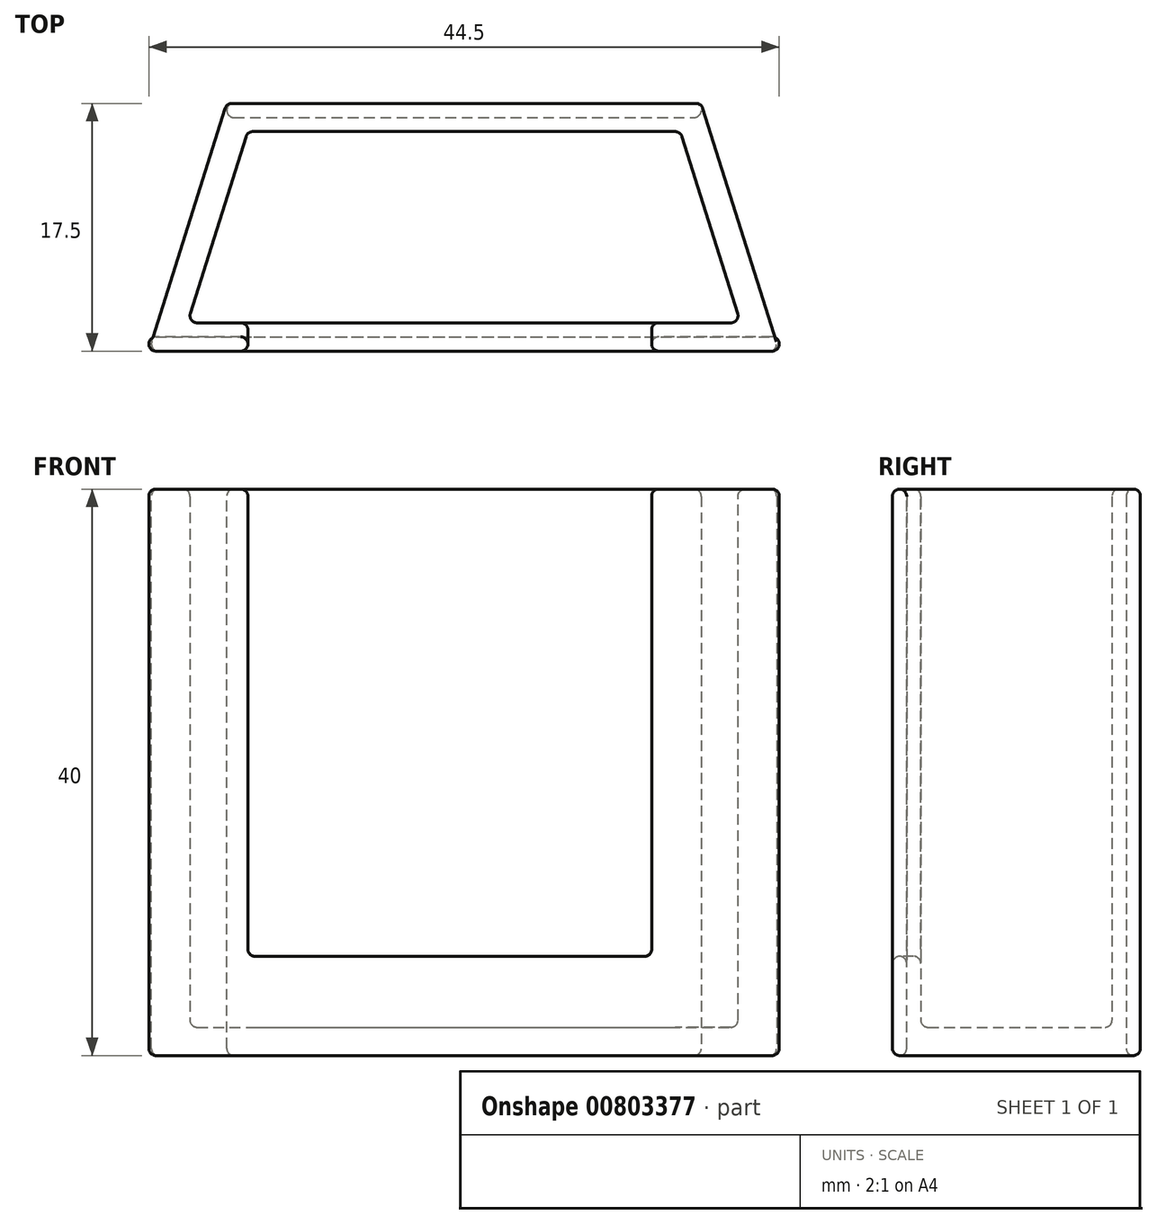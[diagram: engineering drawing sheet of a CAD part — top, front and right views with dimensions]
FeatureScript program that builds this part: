
annotation { "Feature Type Name" : "Feature", "Feature Type Description" : "" }
export const myFeature = defineFeature(function(context is Context, id is Id, definition is map)
    precondition{}
    {
        {
            var Q0;
            Q0=qCreatedBy(makeId("Front.planeOp"),FACE);
            var sketch = newSketch(context, id + "F0", { "sketchPlane" : qUnion([Q0])});
            skLineSegment(sketch, "E0", {"start": v(0, 0) * mm, "end": v(0, 40) * mm});
            skLineSegment(sketch, "E1", {"start": v(0, 0) * mm, "end": v(44.5, 0) * mm});
            skLineSegment(sketch, "E2", {"start": v(44.5, 0) * mm, "end": v(44.5, 40) * mm});
            skLineSegment(sketch, "E3", {"start": v(0, 40) * mm, "end": v(1, 40) * mm});
            skLineSegment(sketch, "E4", {"start": v(44.5, 40) * mm, "end": v(43.5, 40) * mm});
            skLineSegment(sketch, "E5", {"start": v(1, 40) * mm, "end": v(1, 1) * mm});
            skLineSegment(sketch, "E6", {"start": v(1, 1) * mm, "end": v(43.5, 1) * mm});
            skLineSegment(sketch, "E7", {"start": v(43.5, 1) * mm, "end": v(43.5, 40) * mm});
            skPoint(sketch, "E8.end.orphan", {"position": v(32.5, 40) * mm});
            skPoint(sketch, "E9.end.orphan", {"position": v(32.5, 10) * mm});
            skLineSegment(sketch, "E10", {"start": v(44.5, 40) * mm, "end": v(0, 40) * mm});
            skSolve(sketch);
        }
        {
            var Q0;
            Q0 = qSketchRegion(id + "F0", true);
            extrude(context, id + "F1", {"entities" : qUnion([Q0]), "depth" : 1 * mm, "offsetDistance" : 25 * mm});
        }
        {
            var Q0;
            Q0=qCreatedBy(makeId("Front.planeOp"),FACE);
            cPlane(context, id + "F2", {"entities" : qUnion([Q0]), "cplaneType" : CPlaneType.OFFSET, "offset" : 16.5 * mm, "oppositeDirection" : true, "width" : 150 * mm, "height" : 150 * mm});
        }
        {
            var Q0;
            Q0=qCreatedBy(id+"F2.planeOp",FACE);
            var sketch = newSketch(context, id + "F3", { "sketchPlane" : qUnion([Q0])});
            skLineSegment(sketch, "E11", {"start": v(22.25, 0) * mm, "end": v(22.25, 43.45) * mm, "construction": true});
            skLineSegment(sketch, "E12", {"start": v(5.5, 0) * mm, "end": v(39, 0) * mm});
            skPoint(sketch, "E13.orphan", {"position": v(0, 0) * mm});
            skPoint(sketch, "E14.orphan", {"position": v(44.5, 0) * mm});
            skLineSegment(sketch, "E15", {"start": v(5.5, 0) * mm, "end": v(5.5, 40) * mm});
            skLineSegment(sketch, "E16", {"start": v(5.5, 40) * mm, "end": v(39, 40) * mm});
            skLineSegment(sketch, "E17", {"start": v(39, 40) * mm, "end": v(39, 0) * mm});
            skSolve(sketch);
        }
        {
            var Q0;
            Q0 = qSketchRegion(id + "F3", true);
            extrude(context, id + "F4", {"entities" : qUnion([Q0]), "depth" : 1 * mm, "offsetDistance" : 25 * mm});
        }
        {
            var Q0;
            Q0=makeQuery(id+"F4.opExtrude","CAP_FACE",FACE,{"disambiguationData":[OSD([sQuery(id+"F3.wireOp",EDGE,"E12"),sQuery(id+"F3.wireOp",EDGE,"E15"),sQuery(id+"F3.wireOp",EDGE,"E16"),sQuery(id+"F3.wireOp",EDGE,"E17")])],"isStart":true});
            var Q1;
            Q1=makeQuery(id+"F1.opExtrude","CAP_FACE",FACE,{"disambiguationData":[OSD([sQuery(id+"F0.wireOp",EDGE,"E0"),sQuery(id+"F0.wireOp",EDGE,"E1"),sQuery(id+"F0.wireOp",EDGE,"E2"),sQuery(id+"F0.wireOp",EDGE,"E10")])],"isStart":false});
            loft(context, id + "F5", {"sheetProfilesArray" : [{ "sheetProfileEntities" : qUnion([Q0]) }, { "sheetProfileEntities" : qUnion([Q1]) }]});
        }
        {
            var Q0;
            Q0=makeQuery(id+"F5.opLoft","SWEPT_FACE",FACE,{"disambiguationData":[OSD([sQuery(id+"F0.wireOp",EDGE,"E0"),sQuery(id+"F0.wireOp",EDGE,"E2"),sQuery(id+"F0.wireOp",EDGE,"E10"),sQuery(id+"F3.wireOp",EDGE,"E15"),sQuery(id+"F3.wireOp",EDGE,"E16"),sQuery(id+"F3.wireOp",EDGE,"E17")])]});
            shell(context, id + "F6", {"entities" : qUnion([Q0]), "thickness" : 2 * mm});
        }
        {
            var Q0;
            Q0=makeQuery(id+"F1.opExtrude","CAP_FACE",FACE,{"disambiguationData":[OSD([sQuery(id+"F0.wireOp",EDGE,"E0"),sQuery(id+"F0.wireOp",EDGE,"E1"),sQuery(id+"F0.wireOp",EDGE,"E2"),sQuery(id+"F0.wireOp",EDGE,"E10")])],"isStart":false});
            var sketch = newSketch(context, id + "F7", { "sketchPlane" : qUnion([Q0])});
            skLineSegment(sketch, "E18", {"start": v(7, 40) * mm, "end": v(7, 7) * mm});
            skLineSegment(sketch, "E19", {"start": v(7, 7) * mm, "end": v(35.5, 7) * mm});
            skLineSegment(sketch, "E20", {"start": v(35.5, 7) * mm, "end": v(35.5, 40) * mm});
            skLineSegment(sketch, "E21", {"start": v(7, 40) * mm, "end": v(35.5, 40) * mm});
            skPoint(sketch, "E22.0.end.orphan", {"position": v(0, 40) * mm});
            skPoint(sketch, "E22.0.start.orphan", {"position": v(0, 0) * mm});
            skPoint(sketch, "E23.0.end.orphan", {"position": v(44.5, 40) * mm});
            skPoint(sketch, "E23.0.start.orphan", {"position": v(44.5, 0) * mm});
            skSolve(sketch);
        }
        {
            var Q0;
            Q0=makeQuery(id+"F7.imprint","IMPRINT",FACE,{"disambiguationData":[TD([[makeQuery(id+"F7.imprint","IMPRINT",EDGE,{"derivedFrom":sQuery(id+"F7.wireOp",EDGE,"E18")}),1.0]])]});
            var sketch = newSketch(context, id + "F8", { "sketchPlane" : qUnion([Q0])});
            skLineSegment(sketch, "E24.0", {"start": v(35.5, 7) * mm, "end": v(35.5, 40) * mm});
            skLineSegment(sketch, "E24.1", {"start": v(7, 7) * mm, "end": v(35.5, 7) * mm});
            skLineSegment(sketch, "E24.2", {"start": v(7, 40) * mm, "end": v(7, 7) * mm});
            skLineSegment(sketch, "E24.3", {"start": v(7, 40) * mm, "end": v(35.5, 40) * mm});
            skSolve(sketch);
        }
        {
            var Q0;
            Q0 = qSketchRegion(id + "F8", true);
            extrude(context, id + "F9", {"entities" : qUnion([Q0]), "operationType" : NewBodyOperationType.REMOVE, "depth" : -5 * mm, "offsetDistance" : 25 * mm});
        }
        {
            var Q0;
            Q0=makeQuery(id+"F1.opExtrude","CAP_EDGE",EDGE,{"disambiguationData":[OSD([sQuery(id+"F0.wireOp",EDGE,"E1")])],"isStart":false});
            var Q1;
            Q1=makeQuery(id+"F1.opExtrude","SWEPT_FACE",FACE,{"disambiguationData":[OSD([sQuery(id+"F0.wireOp",EDGE,"E1")])]});
            var Q2;
            Q2=makeQuery(id+"F5.opLoft","SWEPT_EDGE",EDGE,{"disambiguationData":[OSD([sQuery(id+"F0.wireOp",EDGE,"E1"),sQuery(id+"F0.wireOp",EDGE,"E2"),sQuery(id+"F3.wireOp",EDGE,"E12"),sQuery(id+"F3.wireOp",EDGE,"E17")])]});
            var Q3;
            Q3=makeQuery(id+"F5.opLoft","SWEPT_FACE",FACE,{"disambiguationData":[OSD([sQuery(id+"F0.wireOp",EDGE,"E0"),sQuery(id+"F0.wireOp",EDGE,"E2"),sQuery(id+"F0.wireOp",EDGE,"E10"),sQuery(id+"F3.wireOp",EDGE,"E15"),sQuery(id+"F3.wireOp",EDGE,"E16"),sQuery(id+"F3.wireOp",EDGE,"E17")])]});
            var Q4;
            Q4=makeQuery(id+"F5.opLoft","SWEPT_FACE",FACE,{"disambiguationData":[OSD([sQuery(id+"F0.wireOp",EDGE,"E0"),sQuery(id+"F0.wireOp",EDGE,"E1"),sQuery(id+"F0.wireOp",EDGE,"E10"),sQuery(id+"F3.wireOp",EDGE,"E12"),sQuery(id+"F3.wireOp",EDGE,"E15"),sQuery(id+"F3.wireOp",EDGE,"E16")])]});
            var Q5;
            Q5=makeQuery(id+"F5.opLoft","SWEPT_EDGE",EDGE,{"disambiguationData":[OSD([sQuery(id+"F0.wireOp",EDGE,"E0"),sQuery(id+"F0.wireOp",EDGE,"E10"),sQuery(id+"F3.wireOp",EDGE,"E15"),sQuery(id+"F3.wireOp",EDGE,"E16")])]});
            var Q6;
            Q6=makeQuery(id+"F5.opLoft","MID_CAP_EDGE",EDGE,{"disambiguationData":[OSD([sQuery(id+"F0.wireOp",EDGE,"E0"),sQuery(id+"F0.wireOp",EDGE,"E1"),sQuery(id+"F0.wireOp",EDGE,"E2")])],"capPos":1.0});
            var Q7;
            Q7=makeQuery(id+"F5.opLoft","SWEPT_FACE",FACE,{"disambiguationData":[OSD([sQuery(id+"F0.wireOp",EDGE,"E0"),sQuery(id+"F0.wireOp",EDGE,"E1"),sQuery(id+"F0.wireOp",EDGE,"E2"),sQuery(id+"F3.wireOp",EDGE,"E12"),sQuery(id+"F3.wireOp",EDGE,"E15"),sQuery(id+"F3.wireOp",EDGE,"E17")])]});
            var Q8;
            Q8=makeQuery(id+"F1.opExtrude","CAP_EDGE",EDGE,{"disambiguationData":[OSD([sQuery(id+"F0.wireOp",EDGE,"E1")])],"isStart":true});
            var Q9;
            Q9=makeQuery(id+"F1.opExtrude","SWEPT_FACE",FACE,{"disambiguationData":[OSD([sQuery(id+"F0.wireOp",EDGE,"E0")])]});
            var Q10;
            Q10=makeQuery(id+"F1.opExtrude","SWEPT_FACE",FACE,{"disambiguationData":[OSD([sQuery(id+"F0.wireOp",EDGE,"E2")])]});
            var Q11;
            Q11=makeQuery(id+"F1.opExtrude","CAP_FACE",FACE,{"disambiguationData":[OSD([sQuery(id+"F0.wireOp",EDGE,"E0"),sQuery(id+"F0.wireOp",EDGE,"E1"),sQuery(id+"F0.wireOp",EDGE,"E2"),sQuery(id+"F0.wireOp",EDGE,"E10")])],"isStart":false});
            var Q12;
            {var subQ0=sQuery(id+"F0.wireOp",EDGE,"E10");Q12=makeQuery(id+"F9.boolean.opBoolean","COPY",FACE,{"disambiguationData":[TD([makeQuery(id+"F1.opExtrude","SWEPT_FACE",FACE,{"disambiguationData":[OSD([subQ0])]})])],"derivedFrom":makeQuery(id+"F9.opExtrude","SWEPT_FACE",FACE,{"disambiguationData":[OSD([sQuery(id+"F8.wireOp",EDGE,"E24.0")])]})});}
            var Q13;
            {var subQ0=sQuery(id+"F0.wireOp",EDGE,"E10");var subQ1=sQuery(id+"F0.wireOp",EDGE,"E2");var subQ2=sQuery(id+"F0.wireOp",EDGE,"E1");var subQ3=sQuery(id+"F0.wireOp",EDGE,"E0");Q13=makeQuery(id+"F9.boolean.opBoolean","COPY",FACE,{"disambiguationData":[TD([makeQuery(id+"F1.opExtrude","CAP_FACE",FACE,{"disambiguationData":[OSD([subQ3,subQ2,subQ1,subQ0])],"isStart":true})])],"derivedFrom":makeQuery(id+"F9.opExtrude","SWEPT_FACE",FACE,{"disambiguationData":[OSD([sQuery(id+"F8.wireOp",EDGE,"E24.1")])]})});}
            var Q14;
            {var subQ0=sQuery(id+"F0.wireOp",EDGE,"E10");Q14=makeQuery(id+"F9.boolean.opBoolean","COPY",FACE,{"disambiguationData":[TD([makeQuery(id+"F1.opExtrude","SWEPT_FACE",FACE,{"disambiguationData":[OSD([subQ0])]})])],"derivedFrom":makeQuery(id+"F9.opExtrude","SWEPT_FACE",FACE,{"disambiguationData":[OSD([sQuery(id+"F8.wireOp",EDGE,"E24.2")])]})});}
            var Q15;
            {var subQ0=sQuery(id+"F8.wireOp",EDGE,"E24.0");Q15=makeQuery(id+"F9.boolean.opBoolean","COPY",EDGE,{"disambiguationData":[topologyDisambiguationEdgeConnected([makeQuery(id+"F1.opExtrude","CAP_FACE",FACE,{"disambiguationData":[OSD([sQuery(id+"F0.wireOp",EDGE,"E0"),sQuery(id+"F0.wireOp",EDGE,"E1"),sQuery(id+"F0.wireOp",EDGE,"E2"),sQuery(id+"F0.wireOp",EDGE,"E10")])],"isStart":false})])],"derivedFrom":makeQuery(id+"F9.opExtrude","CAP_EDGE",EDGE,{"disambiguationData":[OSD([subQ0])],"isStart":true})});}
            var Q16;
            {var subQ0=sQuery(id+"F8.wireOp",EDGE,"E24.1");Q16=makeQuery(id+"F9.boolean.opBoolean","COPY",EDGE,{"disambiguationData":[topologyDisambiguationEdgeConnected([makeQuery(id+"F1.opExtrude","CAP_FACE",FACE,{"disambiguationData":[OSD([sQuery(id+"F0.wireOp",EDGE,"E0"),sQuery(id+"F0.wireOp",EDGE,"E1"),sQuery(id+"F0.wireOp",EDGE,"E2"),sQuery(id+"F0.wireOp",EDGE,"E10")])],"isStart":false})])],"derivedFrom":makeQuery(id+"F9.opExtrude","CAP_EDGE",EDGE,{"disambiguationData":[OSD([subQ0])],"isStart":true})});}
            var Q17;
            {var subQ0=sQuery(id+"F8.wireOp",EDGE,"E24.2");Q17=makeQuery(id+"F9.boolean.opBoolean","COPY",EDGE,{"disambiguationData":[topologyDisambiguationEdgeConnected([makeQuery(id+"F1.opExtrude","CAP_FACE",FACE,{"disambiguationData":[OSD([sQuery(id+"F0.wireOp",EDGE,"E0"),sQuery(id+"F0.wireOp",EDGE,"E1"),sQuery(id+"F0.wireOp",EDGE,"E2"),sQuery(id+"F0.wireOp",EDGE,"E10")])],"isStart":false})])],"derivedFrom":makeQuery(id+"F9.opExtrude","CAP_EDGE",EDGE,{"disambiguationData":[OSD([subQ0])],"isStart":true})});}
            var Q18;
            Q18=makeQuery(id+"F4.opExtrude","SWEPT_FACE",FACE,{"disambiguationData":[OSD([sQuery(id+"F3.wireOp",EDGE,"E12")])]});
            var Q19;
            Q19=makeQuery(id+"F4.opExtrude","CAP_FACE",FACE,{"disambiguationData":[OSD([sQuery(id+"F3.wireOp",EDGE,"E12"),sQuery(id+"F3.wireOp",EDGE,"E15"),sQuery(id+"F3.wireOp",EDGE,"E16"),sQuery(id+"F3.wireOp",EDGE,"E17")])],"isStart":true});
            var Q20;
            Q20=makeQuery(id+"F4.opExtrude","CAP_EDGE",EDGE,{"disambiguationData":[OSD([sQuery(id+"F3.wireOp",EDGE,"E12")])],"isStart":false});
            var Q21;
            Q21=makeQuery(id+"F4.opExtrude","CAP_FACE",FACE,{"disambiguationData":[OSD([sQuery(id+"F3.wireOp",EDGE,"E12"),sQuery(id+"F3.wireOp",EDGE,"E15"),sQuery(id+"F3.wireOp",EDGE,"E16"),sQuery(id+"F3.wireOp",EDGE,"E17")])],"isStart":false});
            var Q22;
            Q22=makeQuery(id+"F4.opExtrude","CAP_EDGE",EDGE,{"disambiguationData":[OSD([sQuery(id+"F3.wireOp",EDGE,"E12")])],"isStart":true});
            var Q23;
            Q23=makeQuery(id+"F4.opExtrude","SWEPT_FACE",FACE,{"disambiguationData":[OSD([sQuery(id+"F3.wireOp",EDGE,"E15")])]});
            var Q24;
            Q24=makeQuery(id+"F6.opShell","OFFSET_EDGE",EDGE,{"disambiguationData":[OSD([sQuery(id+"F0.wireOp",EDGE,"E0"),sQuery(id+"F0.wireOp",EDGE,"E10"),sQuery(id+"F3.wireOp",EDGE,"E15"),sQuery(id+"F3.wireOp",EDGE,"E16")])]});
            var Q25;
            Q25=makeQuery(id+"F6.opShell","OFFSET_EDGE",EDGE,{"disambiguationData":[OSD([sQuery(id+"F0.wireOp",EDGE,"E1"),sQuery(id+"F0.wireOp",EDGE,"E2"),sQuery(id+"F3.wireOp",EDGE,"E12"),sQuery(id+"F3.wireOp",EDGE,"E17")])]});
            var Q26;
            Q26=makeQuery(id+"F6.opShell","OFFSET_FACE",FACE,{"disambiguationData":[OSD([sQuery(id+"F0.wireOp",EDGE,"E0"),sQuery(id+"F0.wireOp",EDGE,"E1"),sQuery(id+"F0.wireOp",EDGE,"E10"),sQuery(id+"F3.wireOp",EDGE,"E12"),sQuery(id+"F3.wireOp",EDGE,"E15"),sQuery(id+"F3.wireOp",EDGE,"E16")])]});
            var Q27;
            Q27=makeQuery(id+"F5.opLoft","CAP_FACE",FACE,{"disambiguationData":[OSD([sQuery(id+"F0.wireOp",EDGE,"E0"),sQuery(id+"F0.wireOp",EDGE,"E1"),sQuery(id+"F0.wireOp",EDGE,"E2"),sQuery(id+"F0.wireOp",EDGE,"E10")])],"isStart":true});
            var Q28;
            Q28=makeQuery(id+"F6.opShell","OFFSET_EDGE",EDGE,{"disambiguationData":[OSD([sQuery(id+"F3.wireOp",EDGE,"E12"),sQuery(id+"F3.wireOp",EDGE,"E15"),sQuery(id+"F3.wireOp",EDGE,"E17")])]});
            var Q29;
            Q29=makeQuery(id+"F5.opLoft","MID_CAP_EDGE",EDGE,{"disambiguationData":[OSD([sQuery(id+"F3.wireOp",EDGE,"E12"),sQuery(id+"F3.wireOp",EDGE,"E15"),sQuery(id+"F3.wireOp",EDGE,"E17")])],"capPos":0.0});
            var Q30;
            Q30=makeQuery(id+"F5.opLoft","SWEPT_EDGE",EDGE,{"disambiguationData":[OSD([sQuery(id+"F0.wireOp",EDGE,"E0"),sQuery(id+"F0.wireOp",EDGE,"E1"),sQuery(id+"F3.wireOp",EDGE,"E12"),sQuery(id+"F3.wireOp",EDGE,"E15")])]});
            var Q31;
            Q31=makeQuery(id+"F6.opShell","OFFSET_FACE",FACE,{"disambiguationData":[OSD([sQuery(id+"F0.wireOp",EDGE,"E0"),sQuery(id+"F0.wireOp",EDGE,"E1"),sQuery(id+"F0.wireOp",EDGE,"E2"),sQuery(id+"F3.wireOp",EDGE,"E12"),sQuery(id+"F3.wireOp",EDGE,"E15"),sQuery(id+"F3.wireOp",EDGE,"E17")])]});
            var Q32;
            Q32=makeQuery(id+"F6.opShell","OFFSET_EDGE",EDGE,{"disambiguationData":[OSD([sQuery(id+"F0.wireOp",EDGE,"E0"),sQuery(id+"F0.wireOp",EDGE,"E1"),sQuery(id+"F0.wireOp",EDGE,"E2")])]});
            var Q33;
            Q33=makeQuery(id+"F5.opLoft","CAP_FACE",FACE,{"disambiguationData":[OSD([sQuery(id+"F3.wireOp",EDGE,"E12"),sQuery(id+"F3.wireOp",EDGE,"E15"),sQuery(id+"F3.wireOp",EDGE,"E16"),sQuery(id+"F3.wireOp",EDGE,"E17")])],"isStart":true});
            var Q34;
            Q34=makeQuery(id+"F5.opLoft","SWEPT_FACE",FACE,{"disambiguationData":[OSD([sQuery(id+"F0.wireOp",EDGE,"E1"),sQuery(id+"F0.wireOp",EDGE,"E2"),sQuery(id+"F0.wireOp",EDGE,"E10"),sQuery(id+"F3.wireOp",EDGE,"E12"),sQuery(id+"F3.wireOp",EDGE,"E16"),sQuery(id+"F3.wireOp",EDGE,"E17")])]});
            var Q35;
            {var subQ0=sQuery(id+"F0.wireOp",EDGE,"E10");var subQ1=sQuery(id+"F0.wireOp",EDGE,"E2");var subQ2=sQuery(id+"F0.wireOp",EDGE,"E0");var subQ3=sQuery(id+"F0.wireOp",EDGE,"E1");Q35=makeQuery(id+"F9.boolean.opBoolean","COPY",FACE,{"disambiguationData":[TD([makeQuery(id+"F5.opLoft","CAP_FACE",FACE,{"disambiguationData":[OSD([subQ2,subQ3,subQ1,subQ0])],"isStart":true})])],"derivedFrom":makeQuery(id+"F9.opExtrude","SWEPT_FACE",FACE,{"disambiguationData":[OSD([sQuery(id+"F8.wireOp",EDGE,"E24.0")])]})});}
            var Q36;
            {var subQ0=sQuery(id+"F0.wireOp",EDGE,"E10");var subQ1=sQuery(id+"F0.wireOp",EDGE,"E2");var subQ2=sQuery(id+"F0.wireOp",EDGE,"E1");var subQ3=sQuery(id+"F0.wireOp",EDGE,"E0");Q36=makeQuery(id+"F9.boolean.opBoolean","COPY",FACE,{"disambiguationData":[TD([makeQuery(id+"F5.opLoft","CAP_FACE",FACE,{"disambiguationData":[OSD([subQ3,subQ2,subQ1,subQ0])],"isStart":true})])],"derivedFrom":makeQuery(id+"F9.opExtrude","SWEPT_FACE",FACE,{"disambiguationData":[OSD([sQuery(id+"F8.wireOp",EDGE,"E24.1")])]})});}
            var Q37;
            {var subQ0=sQuery(id+"F0.wireOp",EDGE,"E10");var subQ1=sQuery(id+"F0.wireOp",EDGE,"E2");var subQ2=sQuery(id+"F0.wireOp",EDGE,"E0");var subQ3=sQuery(id+"F0.wireOp",EDGE,"E1");Q37=makeQuery(id+"F9.boolean.opBoolean","COPY",FACE,{"disambiguationData":[TD([makeQuery(id+"F5.opLoft","CAP_FACE",FACE,{"disambiguationData":[OSD([subQ2,subQ3,subQ1,subQ0])],"isStart":true})])],"derivedFrom":makeQuery(id+"F9.opExtrude","SWEPT_FACE",FACE,{"disambiguationData":[OSD([sQuery(id+"F8.wireOp",EDGE,"E24.2")])]})});}
            var Q38;
            {var subQ0=sQuery(id+"F8.wireOp",EDGE,"E24.0");Q38=makeQuery(id+"F9.boolean.opBoolean","COPY",EDGE,{"disambiguationData":[topologyDisambiguationEdgeConnected([makeQuery(id+"F5.opLoft","CAP_FACE",FACE,{"disambiguationData":[OSD([sQuery(id+"F0.wireOp",EDGE,"E0"),sQuery(id+"F0.wireOp",EDGE,"E1"),sQuery(id+"F0.wireOp",EDGE,"E2"),sQuery(id+"F0.wireOp",EDGE,"E10")])],"isStart":true})])],"derivedFrom":makeQuery(id+"F9.opExtrude","CAP_EDGE",EDGE,{"disambiguationData":[OSD([subQ0])],"isStart":true})});}
            var Q39;
            {var subQ0=sQuery(id+"F8.wireOp",EDGE,"E24.1");Q39=makeQuery(id+"F9.boolean.opBoolean","COPY",EDGE,{"disambiguationData":[topologyDisambiguationEdgeConnected([makeQuery(id+"F5.opLoft","CAP_FACE",FACE,{"disambiguationData":[OSD([sQuery(id+"F0.wireOp",EDGE,"E0"),sQuery(id+"F0.wireOp",EDGE,"E1"),sQuery(id+"F0.wireOp",EDGE,"E2"),sQuery(id+"F0.wireOp",EDGE,"E10")])],"isStart":true})])],"derivedFrom":makeQuery(id+"F9.opExtrude","CAP_EDGE",EDGE,{"disambiguationData":[OSD([subQ0])],"isStart":true})});}
            var Q40;
            {var subQ0=sQuery(id+"F8.wireOp",EDGE,"E24.2");Q40=makeQuery(id+"F9.boolean.opBoolean","COPY",EDGE,{"disambiguationData":[topologyDisambiguationEdgeConnected([makeQuery(id+"F5.opLoft","CAP_FACE",FACE,{"disambiguationData":[OSD([sQuery(id+"F0.wireOp",EDGE,"E0"),sQuery(id+"F0.wireOp",EDGE,"E1"),sQuery(id+"F0.wireOp",EDGE,"E2"),sQuery(id+"F0.wireOp",EDGE,"E10")])],"isStart":true})])],"derivedFrom":makeQuery(id+"F9.opExtrude","CAP_EDGE",EDGE,{"disambiguationData":[OSD([subQ0])],"isStart":true})});}
            var Q41;
            Q41=makeQuery(id+"F1.opExtrude","CAP_EDGE",EDGE,{"disambiguationData":[OSD([sQuery(id+"F0.wireOp",EDGE,"E0")])],"isStart":false});
            var Q42;
            Q42=makeQuery(id+"F1.opExtrude","CAP_EDGE",EDGE,{"disambiguationData":[OSD([sQuery(id+"F0.wireOp",EDGE,"E0")])],"isStart":true});
            var Q43;
            Q43=makeQuery(id+"F1.opExtrude","CAP_EDGE",EDGE,{"disambiguationData":[OSD([sQuery(id+"F0.wireOp",EDGE,"E2")])],"isStart":false});
            var Q44;
            Q44=makeQuery(id+"F1.opExtrude","CAP_FACE",FACE,{"disambiguationData":[OSD([sQuery(id+"F0.wireOp",EDGE,"E0"),sQuery(id+"F0.wireOp",EDGE,"E1"),sQuery(id+"F0.wireOp",EDGE,"E2"),sQuery(id+"F0.wireOp",EDGE,"E10")])],"isStart":true});
            var Q45;
            {var subQ0=sQuery(id+"F0.wireOp",EDGE,"E0");var subQ1=sQuery(id+"F0.wireOp",EDGE,"E10");Q45=makeQuery(id+"F9.boolean.opBoolean","SPLIT",EDGE,{"disambiguationData":[TD([makeQuery(id+"F1.opExtrude","SWEPT_FACE",FACE,{"disambiguationData":[OSD([subQ0])]})])],"derivedFrom":makeQuery(id+"F1.opExtrude","CAP_EDGE",EDGE,{"disambiguationData":[OSD([subQ1])],"isStart":false})});}
            var Q46;
            {var subQ0=sQuery(id+"F0.wireOp",EDGE,"E0");var subQ1=sQuery(id+"F0.wireOp",EDGE,"E10");Q46=makeQuery(id+"F9.boolean.opBoolean","SPLIT",FACE,{"disambiguationData":[TD([makeQuery(id+"F1.opExtrude","SWEPT_FACE",FACE,{"disambiguationData":[OSD([subQ0])]})])],"derivedFrom":makeQuery(id+"F1.opExtrude","SWEPT_FACE",FACE,{"disambiguationData":[OSD([subQ1])]})});}
            var Q47;
            {var subQ0=sQuery(id+"F0.wireOp",EDGE,"E10");var subQ1=sQuery(id+"F0.wireOp",EDGE,"E2");Q47=makeQuery(id+"F9.boolean.opBoolean","SPLIT",FACE,{"disambiguationData":[TD([makeQuery(id+"F1.opExtrude","SWEPT_FACE",FACE,{"disambiguationData":[OSD([subQ1])]})])],"derivedFrom":makeQuery(id+"F1.opExtrude","SWEPT_FACE",FACE,{"disambiguationData":[OSD([subQ0])]})});}
            var Q48;
            Q48=makeQuery(id+"F9.boolean.opBoolean","INTERSECT",EDGE,{"derivedFrom":[makeQuery(id+"F1.opExtrude","CAP_FACE",FACE,{"disambiguationData":[OSD([sQuery(id+"F0.wireOp",EDGE,"E0"),sQuery(id+"F0.wireOp",EDGE,"E1"),sQuery(id+"F0.wireOp",EDGE,"E2"),sQuery(id+"F0.wireOp",EDGE,"E10")])],"isStart":true}),makeQuery(id+"F9.opExtrude","SWEPT_FACE",FACE,{"disambiguationData":[OSD([sQuery(id+"F8.wireOp",EDGE,"E24.0")])]})]});
            var Q49;
            Q49=makeQuery(id+"F4.opExtrude","CAP_EDGE",EDGE,{"disambiguationData":[OSD([sQuery(id+"F3.wireOp",EDGE,"E15")])],"isStart":false});
            var Q50;
            Q50=makeQuery(id+"F6.opShell","OFFSET_FACE",FACE,{"disambiguationData":[OSD([sQuery(id+"F0.wireOp",EDGE,"E1"),sQuery(id+"F0.wireOp",EDGE,"E2"),sQuery(id+"F0.wireOp",EDGE,"E10"),sQuery(id+"F3.wireOp",EDGE,"E12"),sQuery(id+"F3.wireOp",EDGE,"E16"),sQuery(id+"F3.wireOp",EDGE,"E17")])]});
            var Q51;
            Q51=makeQuery(id+"F6.opShell","OFFSET_EDGE",EDGE,{"disambiguationData":[OSD([sQuery(id+"F0.wireOp",EDGE,"E1"),sQuery(id+"F0.wireOp",EDGE,"E2"),sQuery(id+"F0.wireOp",EDGE,"E10")])]});
            var Q52;
            Q52=makeQuery(id+"F6.opShell","OFFSET_EDGE",EDGE,{"disambiguationData":[OSD([sQuery(id+"F0.wireOp",EDGE,"E0"),sQuery(id+"F0.wireOp",EDGE,"E1"),sQuery(id+"F3.wireOp",EDGE,"E12"),sQuery(id+"F3.wireOp",EDGE,"E15")])]});
            var Q53;
            Q53=makeQuery(id+"F5.opLoft","MID_CAP_EDGE",EDGE,{"disambiguationData":[OSD([sQuery(id+"F0.wireOp",EDGE,"E0"),sQuery(id+"F0.wireOp",EDGE,"E1"),sQuery(id+"F0.wireOp",EDGE,"E10")])],"capPos":1.0});
            var Q54;
            Q54=makeQuery(id+"F6.opShell","OFFSET_EDGE",EDGE,{"disambiguationData":[OSD([sQuery(id+"F0.wireOp",EDGE,"E0"),sQuery(id+"F0.wireOp",EDGE,"E1"),sQuery(id+"F0.wireOp",EDGE,"E10")])]});
            var Q55;
            Q55=makeQuery(id+"F5.opLoft","MID_CAP_EDGE",EDGE,{"disambiguationData":[OSD([sQuery(id+"F0.wireOp",EDGE,"E1"),sQuery(id+"F0.wireOp",EDGE,"E2"),sQuery(id+"F0.wireOp",EDGE,"E10")])],"capPos":1.0});
            var Q56;
            Q56=makeQuery(id+"F6.opShell","OFFSET_EDGE",EDGE,{"disambiguationData":[OSD([sQuery(id+"F0.wireOp",EDGE,"E2"),sQuery(id+"F0.wireOp",EDGE,"E10"),sQuery(id+"F3.wireOp",EDGE,"E16"),sQuery(id+"F3.wireOp",EDGE,"E17")])]});
            var Q57;
            Q57=makeQuery(id+"F6.opShell","OFFSET_FACE",FACE,{"disambiguationData":[OSD([sQuery(id+"F3.wireOp",EDGE,"E12"),sQuery(id+"F3.wireOp",EDGE,"E15"),sQuery(id+"F3.wireOp",EDGE,"E16"),sQuery(id+"F3.wireOp",EDGE,"E17")])]});
            var Q58;
            {var subQ2=sQuery(id+"F0.wireOp",EDGE,"E10");var subQ4=sQuery(id+"F0.wireOp",EDGE,"E0");var subQ5=sQuery(id+"F0.wireOp",EDGE,"E2");Q58=makeQuery(id+"F9.boolean.opBoolean","SPLIT",EDGE,{"disambiguationData":[TD([makeQuery(id+"F9.opExtrude","SWEPT_FACE",FACE,{"disambiguationData":[OSD([sQuery(id+"F8.wireOp",EDGE,"E24.2")])]})])],"derivedFrom":makeQuery(id+"F5.opLoft","MID_CAP_EDGE",EDGE,{"disambiguationData":[OSD([subQ4,subQ5,subQ2])],"capPos":1.0})});}
            var Q59;
            Q59=makeQuery(id+"F6.opShell","OFFSET_FACE",FACE,{"disambiguationData":[OSD([sQuery(id+"F0.wireOp",EDGE,"E0"),sQuery(id+"F0.wireOp",EDGE,"E1"),sQuery(id+"F0.wireOp",EDGE,"E2"),sQuery(id+"F0.wireOp",EDGE,"E10")])]});
            var Q60;
            {var subQ2=sQuery(id+"F0.wireOp",EDGE,"E10");var subQ3=sQuery(id+"F0.wireOp",EDGE,"E2");var subQ4=sQuery(id+"F0.wireOp",EDGE,"E0");Q60=makeQuery(id+"F9.boolean.opBoolean","SPLIT",EDGE,{"disambiguationData":[TD([makeQuery(id+"F9.opExtrude","SWEPT_FACE",FACE,{"disambiguationData":[OSD([sQuery(id+"F8.wireOp",EDGE,"E24.0")])]})])],"derivedFrom":makeQuery(id+"F6.opShell","OFFSET_EDGE",EDGE,{"disambiguationData":[OSD([subQ4,subQ3,subQ2])]})});}
            var Q61;
            Q61=makeQuery(id+"F9.boolean.opBoolean","INTERSECT",EDGE,{"derivedFrom":[makeQuery(id+"F6.opShell","OFFSET_FACE",FACE,{"disambiguationData":[OSD([sQuery(id+"F0.wireOp",EDGE,"E0"),sQuery(id+"F0.wireOp",EDGE,"E1"),sQuery(id+"F0.wireOp",EDGE,"E2"),sQuery(id+"F0.wireOp",EDGE,"E10")])]}),makeQuery(id+"F9.opExtrude","SWEPT_FACE",FACE,{"disambiguationData":[OSD([sQuery(id+"F8.wireOp",EDGE,"E24.0")])]})]});
            var Q62;
            Q62=makeQuery(id+"F1.opExtrude","CAP_EDGE",EDGE,{"disambiguationData":[OSD([sQuery(id+"F0.wireOp",EDGE,"E2")])],"isStart":true});
            var Q63;
            {var subQ0=sQuery(id+"F0.wireOp",EDGE,"E10");var subQ1=sQuery(id+"F0.wireOp",EDGE,"E2");Q63=makeQuery(id+"F9.boolean.opBoolean","SPLIT",EDGE,{"disambiguationData":[TD([makeQuery(id+"F1.opExtrude","SWEPT_FACE",FACE,{"disambiguationData":[OSD([subQ1])]})])],"derivedFrom":makeQuery(id+"F1.opExtrude","CAP_EDGE",EDGE,{"disambiguationData":[OSD([subQ0])],"isStart":false})});}
            var Q64;
            Q64=makeQuery(id+"F9.boolean.opBoolean","INTERSECT",EDGE,{"derivedFrom":[makeQuery(id+"F1.opExtrude","CAP_FACE",FACE,{"disambiguationData":[OSD([sQuery(id+"F0.wireOp",EDGE,"E0"),sQuery(id+"F0.wireOp",EDGE,"E1"),sQuery(id+"F0.wireOp",EDGE,"E2"),sQuery(id+"F0.wireOp",EDGE,"E10")])],"isStart":true}),makeQuery(id+"F9.opExtrude","SWEPT_FACE",FACE,{"disambiguationData":[OSD([sQuery(id+"F8.wireOp",EDGE,"E24.1")])]})]});
            var Q65;
            Q65=makeQuery(id+"F9.boolean.opBoolean","INTERSECT",EDGE,{"derivedFrom":[makeQuery(id+"F1.opExtrude","CAP_FACE",FACE,{"disambiguationData":[OSD([sQuery(id+"F0.wireOp",EDGE,"E0"),sQuery(id+"F0.wireOp",EDGE,"E1"),sQuery(id+"F0.wireOp",EDGE,"E2"),sQuery(id+"F0.wireOp",EDGE,"E10")])],"isStart":true}),makeQuery(id+"F9.opExtrude","SWEPT_FACE",FACE,{"disambiguationData":[OSD([sQuery(id+"F8.wireOp",EDGE,"E24.2")])]})]});
            var Q66;
            Q66=makeQuery(id+"F4.opExtrude","SWEPT_EDGE",EDGE,{"disambiguationData":[OSD([sQuery(id+"F3.wireOp",EDGE,"E15"),sQuery(id+"F3.wireOp",EDGE,"E16")])]});
            var Q67;
            Q67=makeQuery(id+"F4.opExtrude","SWEPT_FACE",FACE,{"disambiguationData":[OSD([sQuery(id+"F3.wireOp",EDGE,"E16")])]});
            var Q68;
            Q68=makeQuery(id+"F4.opExtrude","CAP_EDGE",EDGE,{"disambiguationData":[OSD([sQuery(id+"F3.wireOp",EDGE,"E15")])],"isStart":true});
            var Q69;
            Q69=makeQuery(id+"F4.opExtrude","SWEPT_EDGE",EDGE,{"disambiguationData":[OSD([sQuery(id+"F3.wireOp",EDGE,"E12"),sQuery(id+"F3.wireOp",EDGE,"E15")])]});
            var Q70;
            Q70=makeQuery(id+"F4.opExtrude","SWEPT_EDGE",EDGE,{"disambiguationData":[OSD([sQuery(id+"F3.wireOp",EDGE,"E12"),sQuery(id+"F3.wireOp",EDGE,"E17")])]});
            var Q71;
            Q71=makeQuery(id+"F6.opShell","OFFSET_EDGE",EDGE,{"disambiguationData":[OSD([sQuery(id+"F3.wireOp",EDGE,"E12"),sQuery(id+"F3.wireOp",EDGE,"E16"),sQuery(id+"F3.wireOp",EDGE,"E17")])]});
            var Q72;
            Q72=makeQuery(id+"F6.opShell","OFFSET_EDGE",EDGE,{"disambiguationData":[OSD([sQuery(id+"F3.wireOp",EDGE,"E15"),sQuery(id+"F3.wireOp",EDGE,"E16"),sQuery(id+"F3.wireOp",EDGE,"E17")])]});
            var Q73;
            Q73=makeQuery(id+"F6.opShell","OFFSET_EDGE",EDGE,{"disambiguationData":[OSD([sQuery(id+"F3.wireOp",EDGE,"E12"),sQuery(id+"F3.wireOp",EDGE,"E15"),sQuery(id+"F3.wireOp",EDGE,"E16")])]});
            var Q74;
            Q74=makeQuery(id+"F5.opLoft","SWEPT_EDGE",EDGE,{"disambiguationData":[OSD([sQuery(id+"F0.wireOp",EDGE,"E2"),sQuery(id+"F0.wireOp",EDGE,"E10"),sQuery(id+"F3.wireOp",EDGE,"E16"),sQuery(id+"F3.wireOp",EDGE,"E17")])]});
            var Q75;
            Q75=makeQuery(id+"F5.opLoft","MID_CAP_EDGE",EDGE,{"disambiguationData":[OSD([sQuery(id+"F3.wireOp",EDGE,"E12"),sQuery(id+"F3.wireOp",EDGE,"E15"),sQuery(id+"F3.wireOp",EDGE,"E16")])],"capPos":0.0});
            var Q76;
            {var subQ2=sQuery(id+"F0.wireOp",EDGE,"E10");var subQ3=sQuery(id+"F0.wireOp",EDGE,"E2");var subQ4=sQuery(id+"F0.wireOp",EDGE,"E0");Q76=makeQuery(id+"F9.boolean.opBoolean","SPLIT",EDGE,{"disambiguationData":[TD([makeQuery(id+"F9.opExtrude","SWEPT_FACE",FACE,{"disambiguationData":[OSD([sQuery(id+"F8.wireOp",EDGE,"E24.0")])]})])],"derivedFrom":makeQuery(id+"F5.opLoft","MID_CAP_EDGE",EDGE,{"disambiguationData":[OSD([subQ4,subQ3,subQ2])],"capPos":1.0})});}
            var Q77;
            {var subQ2=sQuery(id+"F0.wireOp",EDGE,"E10");var subQ3=sQuery(id+"F0.wireOp",EDGE,"E2");var subQ4=sQuery(id+"F0.wireOp",EDGE,"E0");Q77=makeQuery(id+"F9.boolean.opBoolean","SPLIT",EDGE,{"disambiguationData":[TD([makeQuery(id+"F9.opExtrude","SWEPT_FACE",FACE,{"disambiguationData":[OSD([sQuery(id+"F8.wireOp",EDGE,"E24.2")])]})])],"derivedFrom":makeQuery(id+"F6.opShell","OFFSET_EDGE",EDGE,{"disambiguationData":[OSD([subQ4,subQ3,subQ2])]})});}
            var Q78;
            Q78=makeQuery(id+"F9.boolean.opBoolean","INTERSECT",EDGE,{"derivedFrom":[makeQuery(id+"F6.opShell","OFFSET_FACE",FACE,{"disambiguationData":[OSD([sQuery(id+"F0.wireOp",EDGE,"E0"),sQuery(id+"F0.wireOp",EDGE,"E1"),sQuery(id+"F0.wireOp",EDGE,"E2"),sQuery(id+"F0.wireOp",EDGE,"E10")])]}),makeQuery(id+"F9.opExtrude","SWEPT_FACE",FACE,{"disambiguationData":[OSD([sQuery(id+"F8.wireOp",EDGE,"E24.1")])]})]});
            var Q79;
            Q79=makeQuery(id+"F9.boolean.opBoolean","INTERSECT",EDGE,{"derivedFrom":[makeQuery(id+"F6.opShell","OFFSET_FACE",FACE,{"disambiguationData":[OSD([sQuery(id+"F0.wireOp",EDGE,"E0"),sQuery(id+"F0.wireOp",EDGE,"E1"),sQuery(id+"F0.wireOp",EDGE,"E2"),sQuery(id+"F0.wireOp",EDGE,"E10")])]}),makeQuery(id+"F9.opExtrude","SWEPT_FACE",FACE,{"disambiguationData":[OSD([sQuery(id+"F8.wireOp",EDGE,"E24.2")])]})]});
            var Q80;
            Q80=makeQuery(id+"F1.opExtrude","SWEPT_EDGE",EDGE,{"disambiguationData":[OSD([sQuery(id+"F0.wireOp",EDGE,"E0"),sQuery(id+"F0.wireOp",EDGE,"E10")])]});
            var Q81;
            Q81=makeQuery(id+"F1.opExtrude","SWEPT_EDGE",EDGE,{"disambiguationData":[OSD([sQuery(id+"F0.wireOp",EDGE,"E2"),sQuery(id+"F0.wireOp",EDGE,"E10")])]});
            var Q82;
            Q82=makeQuery(id+"F1.opExtrude","SWEPT_EDGE",EDGE,{"disambiguationData":[OSD([sQuery(id+"F0.wireOp",EDGE,"E1"),sQuery(id+"F0.wireOp",EDGE,"E2")])]});
            var Q83;
            Q83=makeQuery(id+"F1.opExtrude","SWEPT_EDGE",EDGE,{"disambiguationData":[OSD([sQuery(id+"F0.wireOp",EDGE,"E0"),sQuery(id+"F0.wireOp",EDGE,"E1")])]});
            var Q84;
            {var subQ0=sQuery(id+"F8.wireOp",EDGE,"E24.0");Q84=makeQuery(id+"F9.boolean.opBoolean","COPY",EDGE,{"disambiguationData":[topologyDisambiguationEdgeConnected([makeQuery(id+"F1.opExtrude","SWEPT_FACE",FACE,{"disambiguationData":[OSD([sQuery(id+"F0.wireOp",EDGE,"E10")])]})])],"derivedFrom":makeQuery(id+"F9.opExtrude","SWEPT_EDGE",EDGE,{"disambiguationData":[OSD([subQ0,sQuery(id+"F8.wireOp",EDGE,"E24.3")])]})});}
            var Q85;
            {var subQ0=sQuery(id+"F0.wireOp",EDGE,"E0");var subQ1=sQuery(id+"F0.wireOp",EDGE,"E10");Q85=makeQuery(id+"F9.boolean.opBoolean","SPLIT",EDGE,{"disambiguationData":[TD([makeQuery(id+"F1.opExtrude","SWEPT_FACE",FACE,{"disambiguationData":[OSD([subQ0])]})])],"derivedFrom":makeQuery(id+"F1.opExtrude","CAP_EDGE",EDGE,{"disambiguationData":[OSD([subQ1])],"isStart":true})});}
            var Q86;
            {var subQ0=sQuery(id+"F0.wireOp",EDGE,"E10");var subQ1=sQuery(id+"F0.wireOp",EDGE,"E2");Q86=makeQuery(id+"F9.boolean.opBoolean","SPLIT",EDGE,{"disambiguationData":[TD([makeQuery(id+"F1.opExtrude","SWEPT_FACE",FACE,{"disambiguationData":[OSD([subQ1])]})])],"derivedFrom":makeQuery(id+"F1.opExtrude","CAP_EDGE",EDGE,{"disambiguationData":[OSD([subQ0])],"isStart":true})});}
            var Q87;
            {var subQ0=sQuery(id+"F8.wireOp",EDGE,"E24.2");Q87=makeQuery(id+"F9.boolean.opBoolean","COPY",EDGE,{"disambiguationData":[topologyDisambiguationEdgeConnected([makeQuery(id+"F1.opExtrude","SWEPT_FACE",FACE,{"disambiguationData":[OSD([sQuery(id+"F0.wireOp",EDGE,"E10")])]})])],"derivedFrom":makeQuery(id+"F9.opExtrude","SWEPT_EDGE",EDGE,{"disambiguationData":[OSD([subQ0,sQuery(id+"F8.wireOp",EDGE,"E24.3")])]})});}
            var Q88;
            {var subQ0=sQuery(id+"F0.wireOp",EDGE,"E10");var subQ1=sQuery(id+"F0.wireOp",EDGE,"E2");var subQ2=sQuery(id+"F0.wireOp",EDGE,"E1");var subQ3=sQuery(id+"F0.wireOp",EDGE,"E0");var subQ4=sQuery(id+"F8.wireOp",EDGE,"E24.1");var subQ5=sQuery(id+"F8.wireOp",EDGE,"E24.2");Q88=makeQuery(id+"F9.boolean.opBoolean","COPY",EDGE,{"disambiguationData":[TD([makeQuery(id+"F1.opExtrude","CAP_FACE",FACE,{"disambiguationData":[OSD([subQ3,subQ2,subQ1,subQ0])],"isStart":true})])],"derivedFrom":makeQuery(id+"F9.opExtrude","SWEPT_EDGE",EDGE,{"disambiguationData":[OSD([subQ4,subQ5])]})});}
            var Q89;
            {var subQ0=sQuery(id+"F0.wireOp",EDGE,"E10");var subQ1=sQuery(id+"F0.wireOp",EDGE,"E2");var subQ2=sQuery(id+"F0.wireOp",EDGE,"E1");var subQ3=sQuery(id+"F0.wireOp",EDGE,"E0");var subQ4=sQuery(id+"F8.wireOp",EDGE,"E24.1");var subQ5=sQuery(id+"F8.wireOp",EDGE,"E24.0");Q89=makeQuery(id+"F9.boolean.opBoolean","COPY",EDGE,{"disambiguationData":[TD([makeQuery(id+"F1.opExtrude","CAP_FACE",FACE,{"disambiguationData":[OSD([subQ3,subQ2,subQ1,subQ0])],"isStart":true})])],"derivedFrom":makeQuery(id+"F9.opExtrude","SWEPT_EDGE",EDGE,{"disambiguationData":[OSD([subQ5,subQ4])]})});}
            var Q90;
            Q90=makeQuery(id+"F4.opExtrude","CAP_EDGE",EDGE,{"disambiguationData":[OSD([sQuery(id+"F3.wireOp",EDGE,"E16")])],"isStart":true});
            var Q91;
            Q91=makeQuery(id+"F4.opExtrude","SWEPT_FACE",FACE,{"disambiguationData":[OSD([sQuery(id+"F3.wireOp",EDGE,"E17")])]});
            var Q92;
            Q92=makeQuery(id+"F4.opExtrude","CAP_EDGE",EDGE,{"disambiguationData":[OSD([sQuery(id+"F3.wireOp",EDGE,"E17")])],"isStart":true});
            var Q93;
            Q93=makeQuery(id+"F4.opExtrude","CAP_EDGE",EDGE,{"disambiguationData":[OSD([sQuery(id+"F3.wireOp",EDGE,"E16")])],"isStart":false});
            var Q94;
            Q94=makeQuery(id+"F4.opExtrude","CAP_EDGE",EDGE,{"disambiguationData":[OSD([sQuery(id+"F3.wireOp",EDGE,"E17")])],"isStart":false});
            var Q95;
            Q95=makeQuery(id+"F5.opLoft","MID_CAP_EDGE",EDGE,{"disambiguationData":[OSD([sQuery(id+"F3.wireOp",EDGE,"E12"),sQuery(id+"F3.wireOp",EDGE,"E16"),sQuery(id+"F3.wireOp",EDGE,"E17")])],"capPos":0.0});
            var Q96;
            {var subQ0=sQuery(id+"F0.wireOp",EDGE,"E10");var subQ1=sQuery(id+"F0.wireOp",EDGE,"E2");var subQ2=sQuery(id+"F0.wireOp",EDGE,"E1");var subQ3=sQuery(id+"F0.wireOp",EDGE,"E0");var subQ4=sQuery(id+"F8.wireOp",EDGE,"E24.1");var subQ5=sQuery(id+"F8.wireOp",EDGE,"E24.0");Q96=makeQuery(id+"F9.boolean.opBoolean","COPY",EDGE,{"disambiguationData":[TD([makeQuery(id+"F5.opLoft","CAP_FACE",FACE,{"disambiguationData":[OSD([subQ3,subQ2,subQ1,subQ0])],"isStart":true})])],"derivedFrom":makeQuery(id+"F9.opExtrude","SWEPT_EDGE",EDGE,{"disambiguationData":[OSD([subQ5,subQ4])]})});}
            var Q97;
            {var subQ0=sQuery(id+"F8.wireOp",EDGE,"E24.0");Q97=makeQuery(id+"F9.boolean.opBoolean","COPY",EDGE,{"disambiguationData":[topologyDisambiguationEdgeConnected([makeQuery(id+"F5.opLoft","SWEPT_FACE",FACE,{"disambiguationData":[OSD([sQuery(id+"F0.wireOp",EDGE,"E0"),sQuery(id+"F0.wireOp",EDGE,"E2"),sQuery(id+"F0.wireOp",EDGE,"E10"),sQuery(id+"F3.wireOp",EDGE,"E15"),sQuery(id+"F3.wireOp",EDGE,"E16"),sQuery(id+"F3.wireOp",EDGE,"E17")])]})])],"derivedFrom":makeQuery(id+"F9.opExtrude","SWEPT_EDGE",EDGE,{"disambiguationData":[OSD([subQ0,sQuery(id+"F8.wireOp",EDGE,"E24.3")])]})});}
            var Q98;
            Q98=makeQuery(id+"F5.opLoft","MID_CAP_EDGE",EDGE,{"disambiguationData":[OSD([sQuery(id+"F3.wireOp",EDGE,"E15"),sQuery(id+"F3.wireOp",EDGE,"E16"),sQuery(id+"F3.wireOp",EDGE,"E17")])],"capPos":0.0});
            var Q99;
            {var subQ0=sQuery(id+"F8.wireOp",EDGE,"E24.2");Q99=makeQuery(id+"F9.boolean.opBoolean","COPY",EDGE,{"disambiguationData":[topologyDisambiguationEdgeConnected([makeQuery(id+"F5.opLoft","SWEPT_FACE",FACE,{"disambiguationData":[OSD([sQuery(id+"F0.wireOp",EDGE,"E0"),sQuery(id+"F0.wireOp",EDGE,"E2"),sQuery(id+"F0.wireOp",EDGE,"E10"),sQuery(id+"F3.wireOp",EDGE,"E15"),sQuery(id+"F3.wireOp",EDGE,"E16"),sQuery(id+"F3.wireOp",EDGE,"E17")])]})])],"derivedFrom":makeQuery(id+"F9.opExtrude","SWEPT_EDGE",EDGE,{"disambiguationData":[OSD([subQ0,sQuery(id+"F8.wireOp",EDGE,"E24.3")])]})});}
            var Q100;
            {var subQ0=sQuery(id+"F0.wireOp",EDGE,"E10");var subQ1=sQuery(id+"F0.wireOp",EDGE,"E2");var subQ2=sQuery(id+"F0.wireOp",EDGE,"E1");var subQ3=sQuery(id+"F0.wireOp",EDGE,"E0");var subQ4=sQuery(id+"F8.wireOp",EDGE,"E24.1");var subQ5=sQuery(id+"F8.wireOp",EDGE,"E24.2");Q100=makeQuery(id+"F9.boolean.opBoolean","COPY",EDGE,{"disambiguationData":[TD([makeQuery(id+"F5.opLoft","CAP_FACE",FACE,{"disambiguationData":[OSD([subQ3,subQ2,subQ1,subQ0])],"isStart":true})])],"derivedFrom":makeQuery(id+"F9.opExtrude","SWEPT_EDGE",EDGE,{"disambiguationData":[OSD([subQ4,subQ5])]})});}
            var Q101;
            Q101=makeQuery(id+"F4.opExtrude","SWEPT_EDGE",EDGE,{"disambiguationData":[OSD([sQuery(id+"F3.wireOp",EDGE,"E16"),sQuery(id+"F3.wireOp",EDGE,"E17")])]});
            fillet(context, id + "F10", {"entities" : qUnion([Q0, Q1, Q2, Q3, Q4, Q5, Q6, Q7, Q8, Q9, Q10, Q11, Q12, Q13, Q14, Q15, Q16, Q17, Q18, Q19, Q20, Q21, Q22, Q23, Q24, Q25, Q26, Q27, Q28, Q29, Q30, Q31, Q32, Q33, Q34, Q35, Q36, Q37, Q38, Q39, Q40, Q41, Q42, Q43, Q44, Q45, Q46, Q47, Q48, Q49, Q50, Q51, Q52, Q53, Q54, Q55, Q56, Q57, Q58, Q59, Q60, Q61, Q62, Q63, Q64, Q65, Q66, Q67, Q68, Q69, Q70, Q71, Q72, Q73, Q74, Q75, Q76, Q77, Q78, Q79, Q80, Q81, Q82, Q83, Q84, Q85, Q86, Q87, Q88, Q89, Q90, Q91, Q92, Q93, Q94, Q95, Q96, Q97, Q98, Q99, Q100, Q101]), "radius" : 0.5 * mm, "tangentPropagation" : true, "allowEdgeOverflow" : false});
        }
    });
